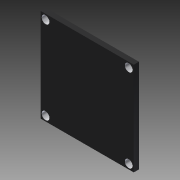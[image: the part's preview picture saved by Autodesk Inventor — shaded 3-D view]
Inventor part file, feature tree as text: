
AUTODESK INVENTOR PART (.ipt)
format: ipt  version: 2015 (Build 190159000, 159)  size: 141,824 bytes
history: native  units: mm
features: extrude x2, sketch x1
ambient origin geometry x8: Origin, YZ Plane, XZ Plane, XY Plane, X Axis, Y Axis, Z Axis, Center Point
bodies: Solid1 (feature_tree)
feature tree (3):
  sketch  "Sketch1"  dims[d0=36.0mm d1=36.0mm d4=3.0mm d5=3.0mm d6=2.0mm d7=0.0mm d8=2.2mm d9=0.0mm]
  extrude  "Extrusion1"  Depth=36.0mm
  extrude  "Extrusion2"  Depth=2.2mm
